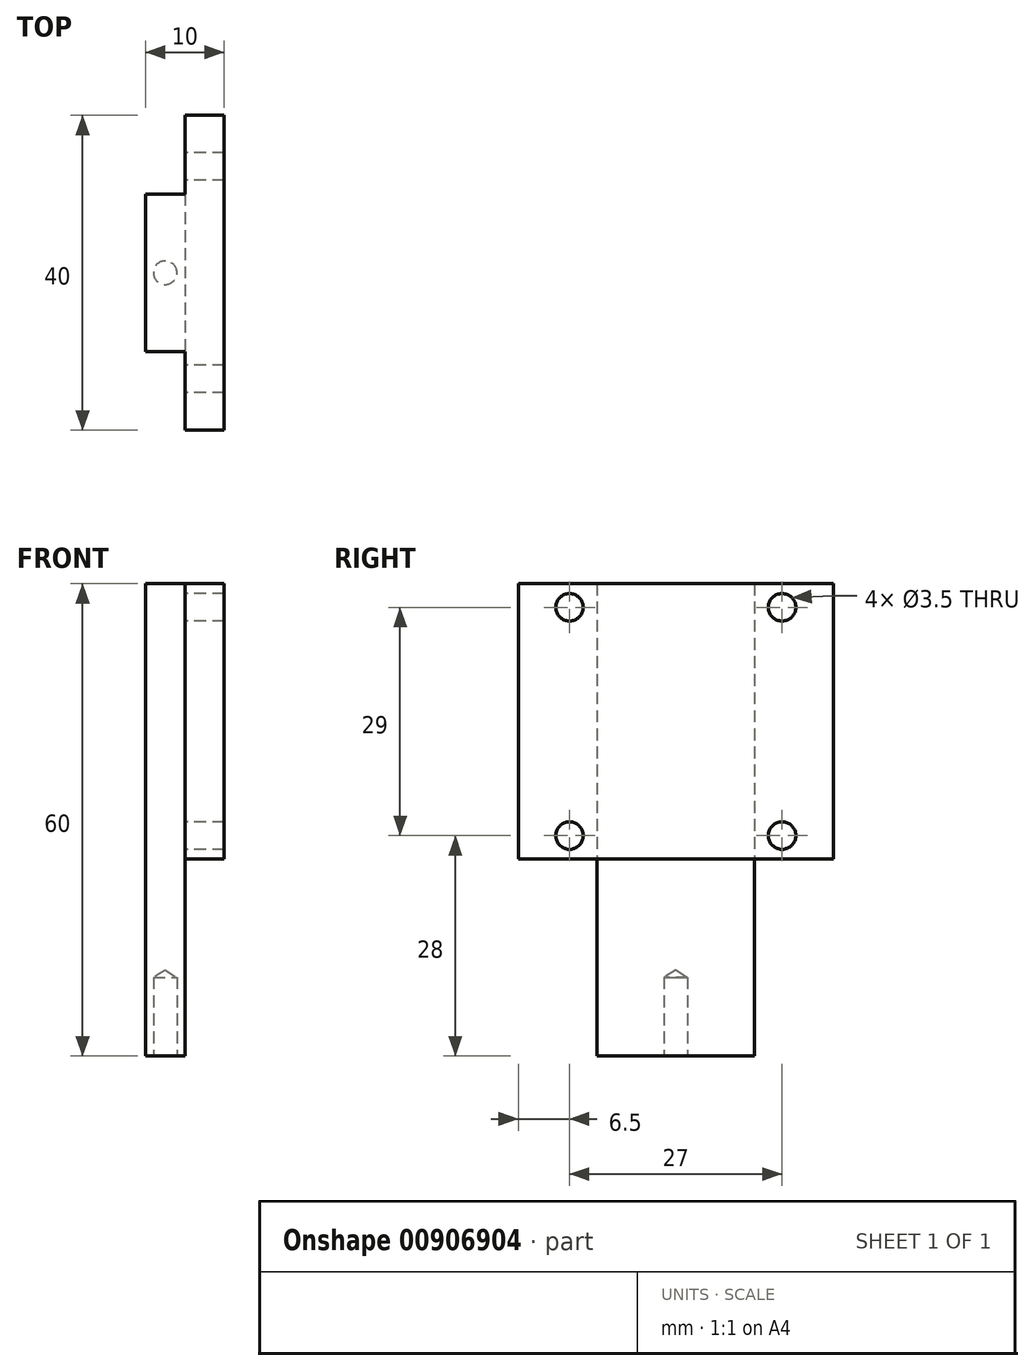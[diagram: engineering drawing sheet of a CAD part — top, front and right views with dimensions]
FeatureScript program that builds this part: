
annotation { "Feature Type Name" : "Feature", "Feature Type Description" : "" }
export const myFeature = defineFeature(function(context is Context, id is Id, definition is map)
    precondition{}
    {
        {
            var Q0;
            Q0=qCreatedBy(makeId("Top.planeOp"),FACE);
            var sketch = newSketch(context, id + "F0", { "sketchPlane" : qUnion([Q0])});
            skLineSegment(sketch, "E0.bottom", {"start": v(2.5, 10) * mm, "end": v(-2.5, 10) * mm});
            skLineSegment(sketch, "E0.top", {"start": v(2.5, -10) * mm, "end": v(-2.5, -10) * mm});
            skLineSegment(sketch, "E0.left", {"start": v(2.5, 10) * mm, "end": v(2.5, -10) * mm});
            skLineSegment(sketch, "E0.right", {"start": v(-2.5, 10) * mm, "end": v(-2.5, -10) * mm});
            skPoint(sketch, "E0.middle", {"position": v(0, 0) * mm});
            skSolve(sketch);
        }
        {
            var Q0;
            Q0=makeQuery(id+"F0.imprint","IMPRINT",FACE,{"disambiguationData":[TD([[makeQuery(id+"F0.imprint","IMPRINT",EDGE,{"derivedFrom":sQuery(id+"F0.wireOp",EDGE,"E0.bottom")}),1.0]])]});
            extrude(context, id + "F1", {"entities" : qUnion([Q0]), "depth" : 60 * mm, "offsetDistance" : 25 * mm});
        }
        {
            var Q0;
            Q0=makeQuery(id+"F1.opExtrude","SWEPT_FACE",FACE,{"disambiguationData":[OSD([sQuery(id+"F0.wireOp",EDGE,"E0.left")])]});
            var sketch = newSketch(context, id + "F2", { "sketchPlane" : qUnion([Q0])});
            skLineSegment(sketch, "E1.bottom", {"start": v(20, 60) * mm, "end": v(-20, 60) * mm});
            skLineSegment(sketch, "E1.top", {"start": v(20, 25) * mm, "end": v(-20, 25) * mm});
            skLineSegment(sketch, "E1.left", {"start": v(20, 60) * mm, "end": v(20, 25) * mm});
            skLineSegment(sketch, "E1.right", {"start": v(-20, 60) * mm, "end": v(-20, 25) * mm});
            skPoint(sketch, "E1.middle", {"position": v(0, 42.5) * mm});
            skCircle(sketch, "E2", {"center": v(-13.5, 57) * mm, "radius": 1.75 * mm});
            skLineSegment(sketch, "E3", {"start": v(-20, 42.5) * mm, "end": v(20, 42.5) * mm, "construction": true});
            skCircle(sketch, "E4.MirrorC", {"center": v(13.5, 57) * mm, "radius": 1.75 * mm});
            skLineSegment(sketch, "E5.MirrorCS", {"start": v(20, 42.5) * mm, "end": v(-20, 42.5) * mm, "construction": true});
            skCircle(sketch, "E6.MirrorC", {"center": v(-13.5, 28) * mm, "radius": 1.75 * mm});
            skCircle(sketch, "E7.MirrorC", {"center": v(13.5, 28) * mm, "radius": 1.75 * mm});
            skSolve(sketch);
        }
        {
            var Q0;
            {var subQ0=sQuery(id+"F2.wireOp",EDGE,"E1.left");Q0=makeQuery(id+"F2.imprint","IMPRINT",FACE,{"disambiguationData":[TD([[makeQuery(id+"F2.imprint","IMPRINT",EDGE,{"derivedFrom":subQ0}),-1.0]])]});}
            var Q1;
            {var subQ0=sQuery(id+"F2.wireOp",EDGE,"E1.right");Q1=makeQuery(id+"F2.imprint","IMPRINT",FACE,{"disambiguationData":[TD([[makeQuery(id+"F2.imprint","IMPRINT",EDGE,{"derivedFrom":subQ0}),1.0]])]});}
            var Q2;
            {var subQ0=sQuery(id+"F2.wireOp",EDGE,"E1.bottom");var subQ1=sQuery(id+"F0.wireOp",EDGE,"E0.left");var subQ2=makeQuery(id+"F1.opExtrude","SWEPT_EDGE",EDGE,{"disambiguationData":[OSD([sQuery(id+"F0.wireOp",EDGE,"E0.bottom"),subQ1])]});var subQ3=makeQuery(id+"F2.imprint","INTERSECT",VERTEX,{"derivedFrom":[subQ2,subQ0]});Q2=makeQuery(id+"F2.imprint","IMPRINT",FACE,{"disambiguationData":[TD([[makeQuery(id+"F2.imprint","IMPRINT",EDGE,{"disambiguationData":[TD([[subQ3,-1.0]])],"derivedFrom":subQ0}),1.0]])]});}
            extrude(context, id + "F3", {"entities" : qUnion([Q0, Q1, Q2]), "operationType" : NewBodyOperationType.ADD, "depth" : 5 * mm, "offsetDistance" : 25 * mm});
        }
        {
            var Q0;
            Q0=makeQuery(id+"F1.opExtrude","CAP_FACE",FACE,{"disambiguationData":[OSD([sQuery(id+"F0.wireOp",EDGE,"E0.bottom"),sQuery(id+"F0.wireOp",EDGE,"E0.top"),sQuery(id+"F0.wireOp",EDGE,"E0.left"),sQuery(id+"F0.wireOp",EDGE,"E0.right")])],"isStart":true});
            var sketch = newSketch(context, id + "F4", { "sketchPlane" : qUnion([Q0])});
            skCircle(sketch, "E8", {"center": v(0, 0) * mm, "radius": 1.75 * mm});
            skSolve(sketch);
        }
        {
            var Q0;
            Q0=sQuery(id+"F4.wireOp",VERTEX,"E8.center");
            var Q1;
            Q1=makeQuery(id+"F1.opExtrude","SWEPT_BODY",BODY,{"disambiguationData":[OSD([sQuery(id+"F0.wireOp",EDGE,"E0.bottom"),sQuery(id+"F0.wireOp",EDGE,"E0.top"),sQuery(id+"F0.wireOp",EDGE,"E0.left"),sQuery(id+"F0.wireOp",EDGE,"E0.right")])]});
            hole(context, id + "F5", {"style" : HoleStyle.SIMPLE, "endStyle" : HoleEndStyle.BLIND, "standardTappedOrClearance" : lookupTablePath({ "standard" : "ISO", "size" : "3", "type" : "Drilled" }), "standardBlindInLast" : lookupTablePath({ "standard" : "ISO", "size" : "3", "type" : "Drilled" }), "holeDiameter" : 3 * mm, "majorDiameter" : 5 * mm, "holeDepth" : 10 * mm, "isTappedThrough" : true, "tappedDepth" : 12 * mm, "tapClearance" : 3, "locations" : qUnion([Q0]), "scope" : qUnion([Q1])});
        }
    });
